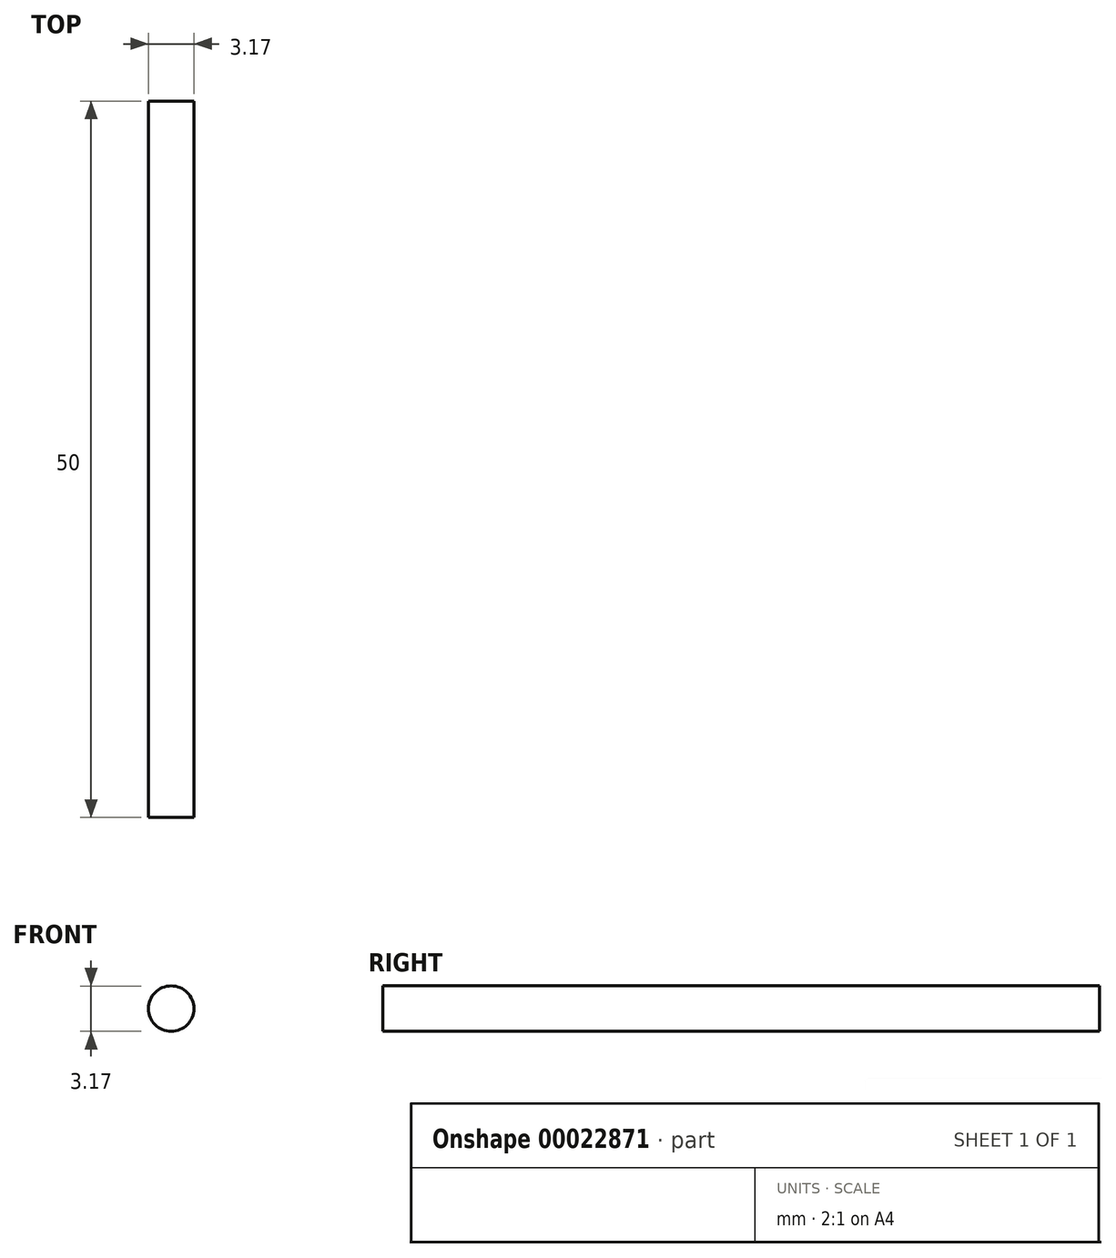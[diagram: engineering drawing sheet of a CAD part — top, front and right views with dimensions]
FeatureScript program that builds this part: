
annotation { "Feature Type Name" : "Feature", "Feature Type Description" : "" }
export const myFeature = defineFeature(function(context is Context, id is Id, definition is map)
    precondition{}
    {
        {
            var Q0;
            Q0=qCreatedBy(makeId("Front.planeOp"),FACE);
            var sketch = newSketch(context, id + "F0", { "sketchPlane" : qUnion([Q0])});
            skCircle(sketch, "E0", {"center": v(-4.7, 10.7) * mm, "radius": 1.59 * mm});
            skSolve(sketch);
        }
        {
            var Q0;
            Q0=makeQuery(id+"F0.imprint","IMPRINT",FACE,{"disambiguationData":[TD([[makeQuery(id+"F0.imprint","IMPRINT",EDGE,{"derivedFrom":sQuery(id+"F0.wireOp",EDGE,"E0")}),1.0]])]});
            extrude(context, id + "F1", {"entities" : qUnion([Q0]), "depth" : 50 * mm});
        }
    });
